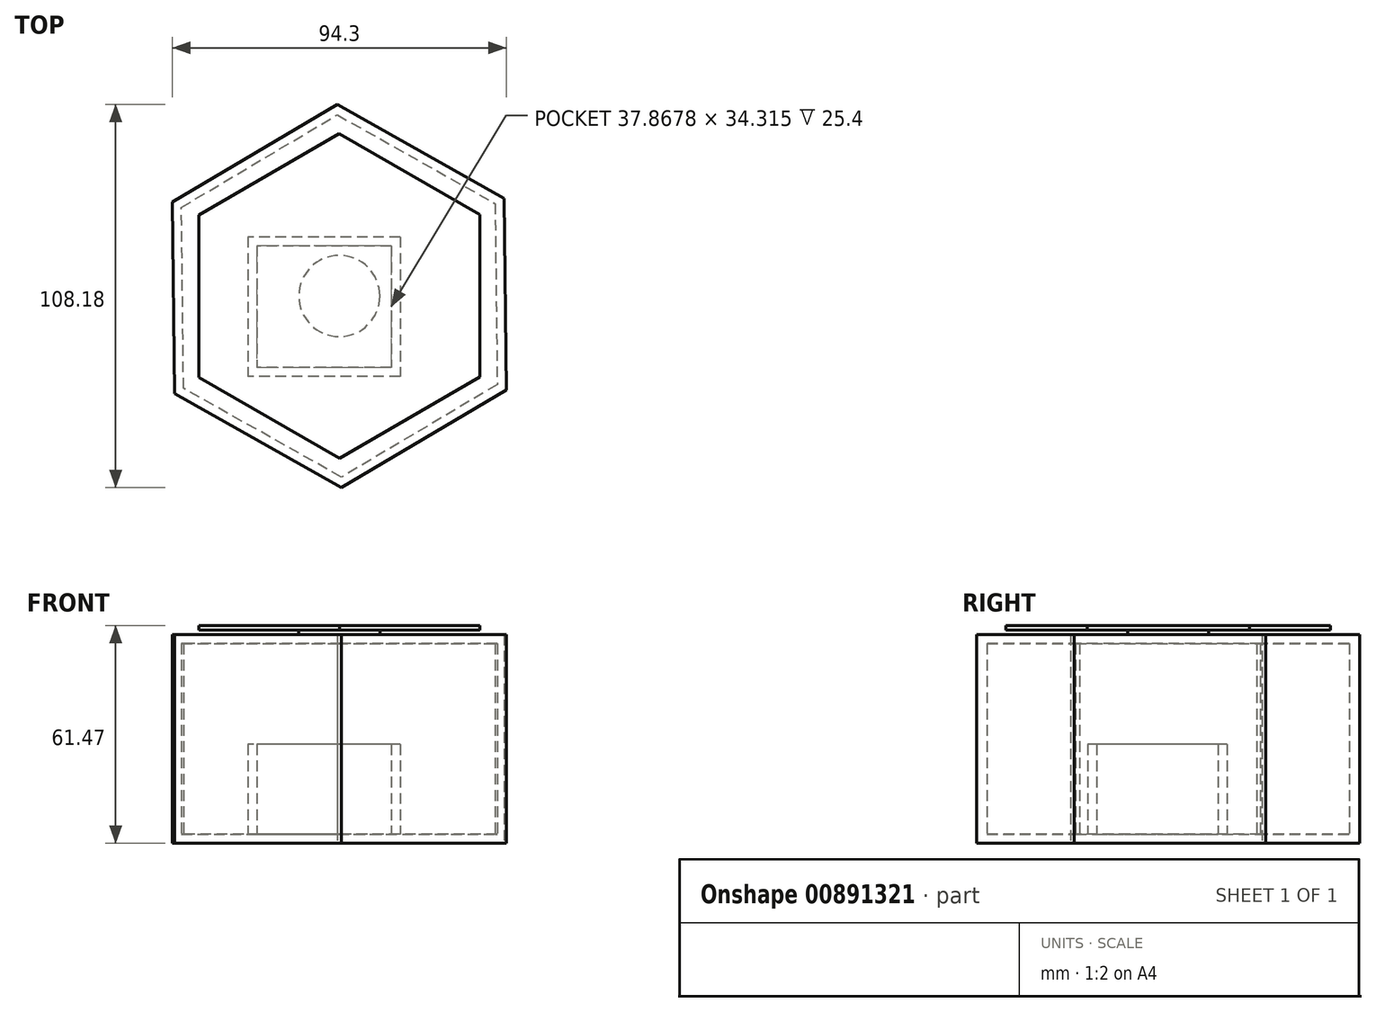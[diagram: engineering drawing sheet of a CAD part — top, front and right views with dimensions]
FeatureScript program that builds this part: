
annotation { "Feature Type Name" : "Feature", "Feature Type Description" : "" }
export const myFeature = defineFeature(function(context is Context, id is Id, definition is map)
    precondition{}
    {
        {
            var Q0;
            Q0=qCreatedBy(makeId("Top.planeOp"),FACE);
            var sketch = newSketch(context, id + "F0", { "sketchPlane" : qUnion([Q0])});
            skCircle(sketch, "E0.cCircle", {"center": v(0, 0) * mm, "radius": 46.84 * mm, "construction": true});
            skLineSegment(sketch, "E0.0", {"start": v(-0.62, 54.09) * mm, "end": v(46.53, 27.58) * mm});
            skLineSegment(sketch, "E0.1", {"start": v(46.53, 27.58) * mm, "end": v(47.15, -26.5) * mm});
            skLineSegment(sketch, "E0.2", {"start": v(47.15, -26.5) * mm, "end": v(0.62, -54.09) * mm});
            skLineSegment(sketch, "E0.3", {"start": v(0.62, -54.09) * mm, "end": v(-46.53, -27.58) * mm});
            skLineSegment(sketch, "E0.4", {"start": v(-46.53, -27.58) * mm, "end": v(-47.15, 26.5) * mm});
            skLineSegment(sketch, "E0.5", {"start": v(-47.15, 26.5) * mm, "end": v(-0.62, 54.09) * mm});
            skPoint(sketch, "E0.0.midPoint", {"position": v(22.95, 40.83) * mm});
            skSolve(sketch);
        }
        {
            var Q0;
            Q0 = qSketchRegion(id + "F0", true);
            extrude(context, id + "F1", {"entities" : qUnion([Q0]), "depth" : 56.4 * mm, "offsetDistance" : 25.4 * mm});
        }
        {
            var Q0;
            Q0=makeQuery(id+"F1.opExtrude","CAP_FACE",FACE,{"disambiguationData":[OSD([sQuery(id+"F0.wireOp",EDGE,"E0.0"),sQuery(id+"F0.wireOp",EDGE,"E0.1"),sQuery(id+"F0.wireOp",EDGE,"E0.2"),sQuery(id+"F0.wireOp",EDGE,"E0.3"),sQuery(id+"F0.wireOp",EDGE,"E0.4"),sQuery(id+"F0.wireOp",EDGE,"E0.5")])],"isStart":false});
            shell(context, id + "F2", {"entities" : qUnion([Q0]), "thickness" : 2.54 * mm});
        }
        {
            var Q0;
            Q0=makeQuery(id+"F2.opShell","OFFSET_FACE",FACE,{"disambiguationData":[OSD([sQuery(id+"F0.wireOp",EDGE,"E0.0"),sQuery(id+"F0.wireOp",EDGE,"E0.1"),sQuery(id+"F0.wireOp",EDGE,"E0.2"),sQuery(id+"F0.wireOp",EDGE,"E0.3"),sQuery(id+"F0.wireOp",EDGE,"E0.4"),sQuery(id+"F0.wireOp",EDGE,"E0.5")])]});
            var sketch = newSketch(context, id + "F3", { "sketchPlane" : qUnion([Q0])});
            skLineSegment(sketch, "E1.bottom", {"start": v(17.18, 16.7) * mm, "end": v(-25.77, 16.7) * mm});
            skLineSegment(sketch, "E1.top", {"start": v(17.18, -22.7) * mm, "end": v(-25.77, -22.7) * mm});
            skLineSegment(sketch, "E1.left", {"start": v(17.18, 16.7) * mm, "end": v(17.18, -22.7) * mm});
            skLineSegment(sketch, "E1.right", {"start": v(-25.77, 16.7) * mm, "end": v(-25.77, -22.7) * mm});
            skSolve(sketch);
        }
        {
            var Q0;
            Q0 = qSketchRegion(id + "F3", true);
            extrude(context, id + "F4", {"entities" : qUnion([Q0]), "operationType" : NewBodyOperationType.ADD, "depth" : 25.4 * mm, "offsetDistance" : 25.4 * mm});
        }
        {
            var Q0;
            Q0=makeQuery(id+"F4.opExtrude","CAP_FACE",FACE,{"disambiguationData":[OSD([sQuery(id+"F3.wireOp",EDGE,"E1.bottom"),sQuery(id+"F3.wireOp",EDGE,"E1.top"),sQuery(id+"F3.wireOp",EDGE,"E1.left"),sQuery(id+"F3.wireOp",EDGE,"E1.right")])],"isStart":false});
            shell(context, id + "F5", {"entities" : qUnion([Q0]), "thickness" : 2.54 * mm});
        }
        {
            var Q0;
            Q0=makeQuery(id+"F1.opExtrude","CAP_FACE",FACE,{"disambiguationData":[OSD([sQuery(id+"F0.wireOp",EDGE,"E0.0"),sQuery(id+"F0.wireOp",EDGE,"E0.1"),sQuery(id+"F0.wireOp",EDGE,"E0.2"),sQuery(id+"F0.wireOp",EDGE,"E0.3"),sQuery(id+"F0.wireOp",EDGE,"E0.4"),sQuery(id+"F0.wireOp",EDGE,"E0.5")])],"isStart":false});
            var sketch = newSketch(context, id + "F6", { "sketchPlane" : qUnion([Q0])});
            skCircle(sketch, "E2.cCircle", {"center": v(0, 0) * mm, "radius": 46.84 * mm, "construction": true});
            skLineSegment(sketch, "E2.0", {"start": v(-0.62, 54.09) * mm, "end": v(46.53, 27.58) * mm});
            skLineSegment(sketch, "E2.1", {"start": v(46.53, 27.58) * mm, "end": v(47.15, -26.5) * mm});
            skLineSegment(sketch, "E2.2", {"start": v(47.15, -26.5) * mm, "end": v(0.62, -54.09) * mm});
            skLineSegment(sketch, "E2.3", {"start": v(0.62, -54.09) * mm, "end": v(-46.53, -27.58) * mm});
            skLineSegment(sketch, "E2.4", {"start": v(-46.53, -27.58) * mm, "end": v(-47.15, 26.5) * mm});
            skLineSegment(sketch, "E2.5", {"start": v(-47.15, 26.5) * mm, "end": v(-0.62, 54.09) * mm});
            skPoint(sketch, "E2.0.midPoint", {"position": v(22.95, 40.83) * mm});
            skSolve(sketch);
        }
        {
            var Q0;
            Q0 = qSketchRegion(id + "F6", true);
            extrude(context, id + "F7", {"entities" : qUnion([Q0]), "operationType" : NewBodyOperationType.ADD, "depth" : 2.54 * mm, "offsetDistance" : 25.4 * mm});
        }
        {
            var Q0;
            Q0=makeQuery(id+"F7.opExtrude","CAP_FACE",FACE,{"disambiguationData":[OSD([sQuery(id+"F6.wireOp",EDGE,"E2.0"),sQuery(id+"F6.wireOp",EDGE,"E2.1"),sQuery(id+"F6.wireOp",EDGE,"E2.2"),sQuery(id+"F6.wireOp",EDGE,"E2.3"),sQuery(id+"F6.wireOp",EDGE,"E2.4"),sQuery(id+"F6.wireOp",EDGE,"E2.5")])],"isStart":false});
            var sketch = newSketch(context, id + "F8", { "sketchPlane" : qUnion([Q0])});
            skCircle(sketch, "E3", {"center": v(0, 0) * mm, "radius": 11.45 * mm});
            skSolve(sketch);
        }
        {
            var Q0;
            Q0 = qSketchRegion(id + "F8", true);
            extrude(context, id + "F9", {"entities" : qUnion([Q0]), "operationType" : NewBodyOperationType.ADD, "depth" : 1.27 * mm, "offsetDistance" : 25.4 * mm});
        }
        {
            var Q0;
            Q0=makeQuery(id+"F9.opExtrude","CAP_FACE",FACE,{"disambiguationData":[OSD([sQuery(id+"F8.wireOp",EDGE,"E3")])],"isStart":false});
            var sketch = newSketch(context, id + "F10", { "sketchPlane" : qUnion([Q0])});
            skCircle(sketch, "E4.cCircle", {"center": v(0, 0) * mm, "radius": 39.68 * mm, "construction": true});
            skLineSegment(sketch, "E4.0", {"start": v(-0.03, 45.82) * mm, "end": v(39.67, 22.94) * mm});
            skLineSegment(sketch, "E4.1", {"start": v(39.67, 22.94) * mm, "end": v(39.7, -22.88) * mm});
            skLineSegment(sketch, "E4.2", {"start": v(39.7, -22.88) * mm, "end": v(0.03, -45.82) * mm});
            skLineSegment(sketch, "E4.3", {"start": v(0.03, -45.82) * mm, "end": v(-39.67, -22.94) * mm});
            skLineSegment(sketch, "E4.4", {"start": v(-39.67, -22.94) * mm, "end": v(-39.7, 22.88) * mm});
            skLineSegment(sketch, "E4.5", {"start": v(-39.7, 22.88) * mm, "end": v(-0.03, 45.82) * mm});
            skPoint(sketch, "E4.0.midPoint", {"position": v(19.82, 34.38) * mm});
            skSolve(sketch);
        }
        {
            var Q0;
            Q0 = qSketchRegion(id + "F10", true);
            extrude(context, id + "F11", {"entities" : qUnion([Q0]), "operationType" : NewBodyOperationType.ADD, "depth" : 1.27 * mm, "offsetDistance" : 25.4 * mm});
        }
    });
